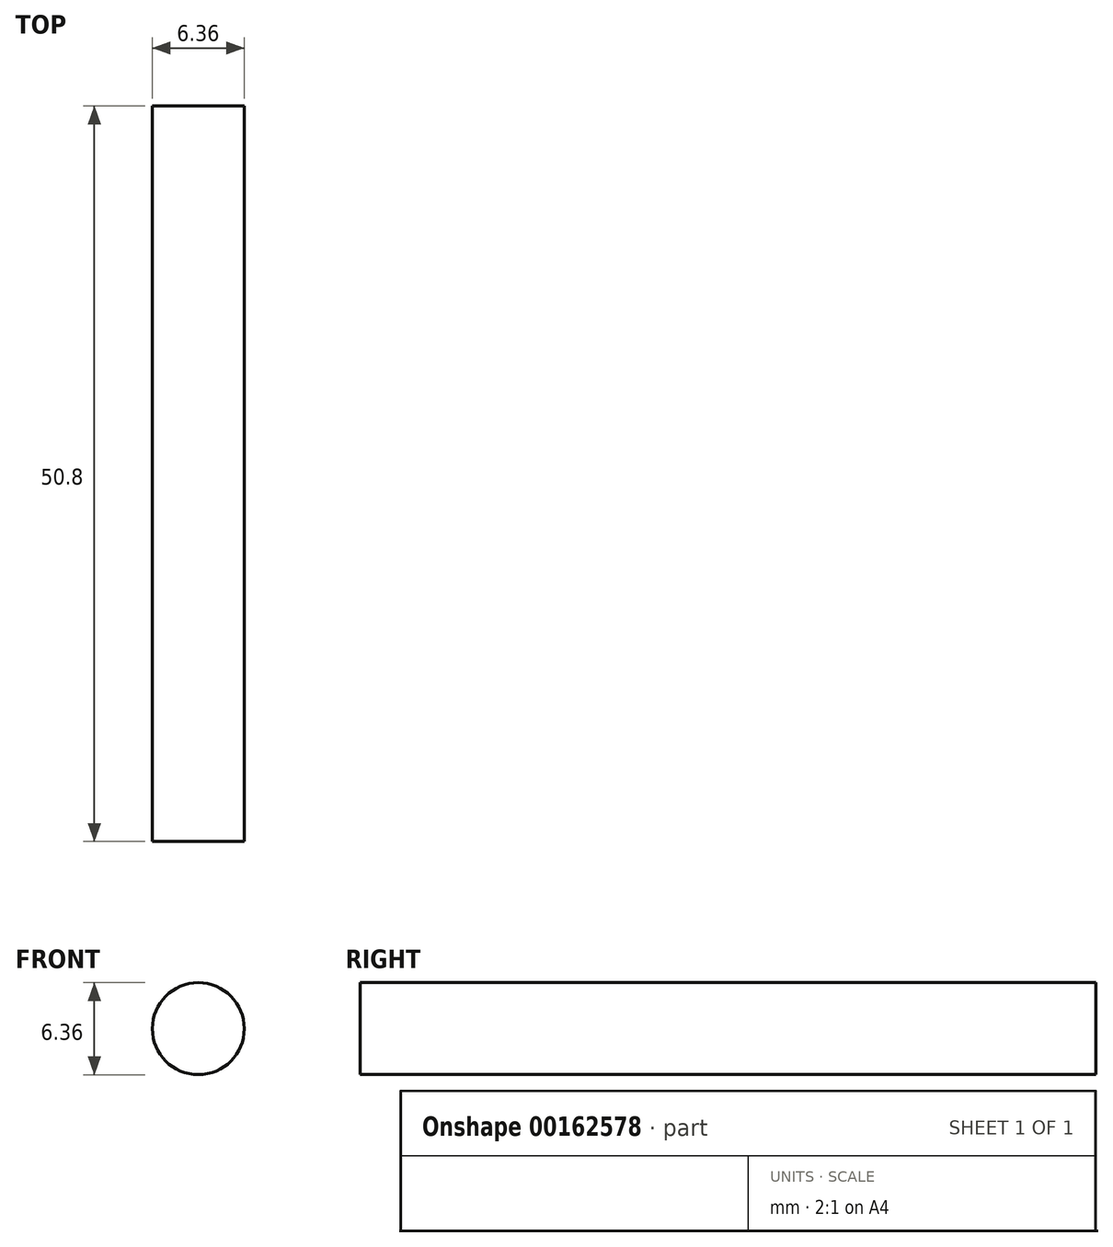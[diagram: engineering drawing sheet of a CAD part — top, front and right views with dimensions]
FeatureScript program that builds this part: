
annotation { "Feature Type Name" : "Feature", "Feature Type Description" : "" }
export const myFeature = defineFeature(function(context is Context, id is Id, definition is map)
    precondition{}
    {
        {
            var Q0;
            Q0=qCreatedBy(makeId("Front.planeOp"),FACE);
            var sketch = newSketch(context, id + "F0", { "sketchPlane" : qUnion([Q0])});
            skCircle(sketch, "E0", {"center": v(0, 0) * mm, "radius": 3.18 * mm});
            skSolve(sketch);
        }
        {
            var Q0;
            Q0 = qSketchRegion(id + "F0", true);
            extrude(context, id + "F1", {"entities" : qUnion([Q0]), "depth" : 50.8 * mm});
        }
    });
